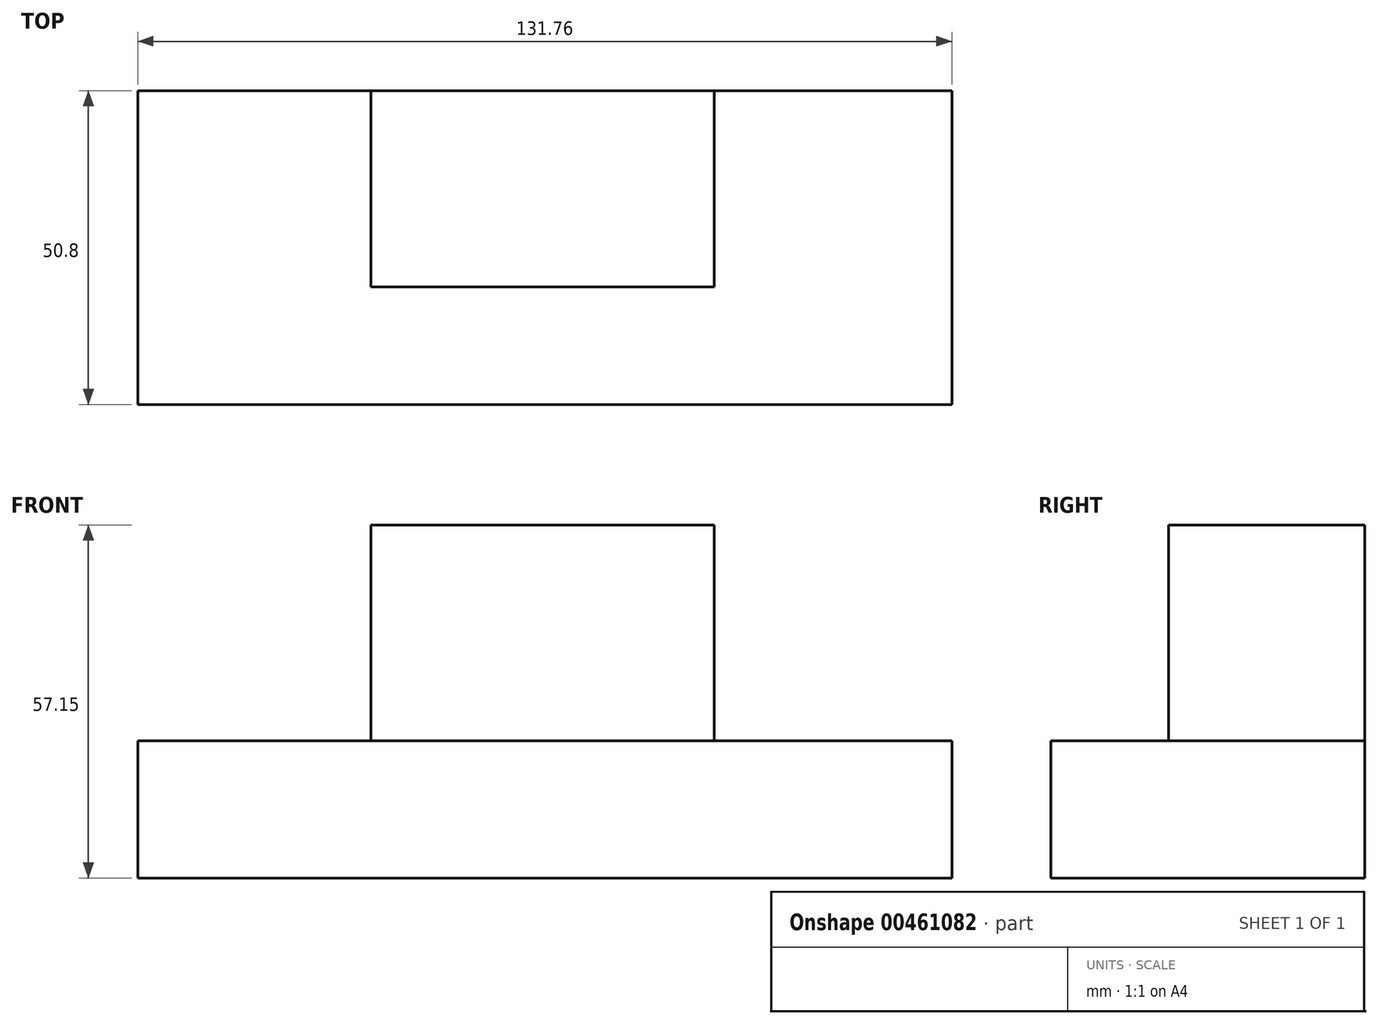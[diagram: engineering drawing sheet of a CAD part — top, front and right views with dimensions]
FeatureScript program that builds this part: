
annotation { "Feature Type Name" : "Feature", "Feature Type Description" : "" }
export const myFeature = defineFeature(function(context is Context, id is Id, definition is map)
    precondition{}
    {
        {
            var Q0;
            Q0=qCreatedBy(makeId("Top.planeOp"),FACE);
            var sketch = newSketch(context, id + "F0", { "sketchPlane" : qUnion([Q0])});
            skLineSegment(sketch, "E0.bottom", {"start": v(0, 0) * mm, "end": v(131.76, 0) * mm});
            skLineSegment(sketch, "E0.top", {"start": v(0, -50.8) * mm, "end": v(131.76, -50.8) * mm});
            skLineSegment(sketch, "E0.left", {"start": v(0, 0) * mm, "end": v(0, -50.8) * mm});
            skLineSegment(sketch, "E0.right", {"start": v(131.76, 0) * mm, "end": v(131.76, -50.8) * mm});
            skSolve(sketch);
        }
        {
            var Q0;
            Q0 = qSketchRegion(id + "F0", true);
            extrude(context, id + "F1", {"entities" : qUnion([Q0]), "depth" : 22.22 * mm});
        }
        {
            var Q0;
            Q0=makeQuery(id+"F1.opExtrude","CAP_FACE",FACE,{"disambiguationData":[OSD([sQuery(id+"F0.wireOp",EDGE,"E0.bottom"),sQuery(id+"F0.wireOp",EDGE,"E0.top"),sQuery(id+"F0.wireOp",EDGE,"E0.left"),sQuery(id+"F0.wireOp",EDGE,"E0.right")])],"isStart":false});
            var sketch = newSketch(context, id + "F2", { "sketchPlane" : qUnion([Q0])});
            skLineSegment(sketch, "E1", {"start": v(0, -25.4) * mm, "end": v(38.1, -25.4) * mm});
            skLineSegment(sketch, "E2.bottom", {"start": v(37.7, 0) * mm, "end": v(93.27, 0) * mm});
            skLineSegment(sketch, "E2.top", {"start": v(37.7, -31.75) * mm, "end": v(93.27, -31.75) * mm});
            skLineSegment(sketch, "E2.left", {"start": v(37.7, 0) * mm, "end": v(37.7, -31.75) * mm});
            skLineSegment(sketch, "E2.right", {"start": v(93.27, 0) * mm, "end": v(93.27, -31.75) * mm});
            skSolve(sketch);
        }
        {
            var Q0;
            Q0 = qSketchRegion(id + "F2", true);
            extrude(context, id + "F3", {"entities" : qUnion([Q0]), "operationType" : NewBodyOperationType.ADD, "depth" : 34.92 * mm});
        }
    });
